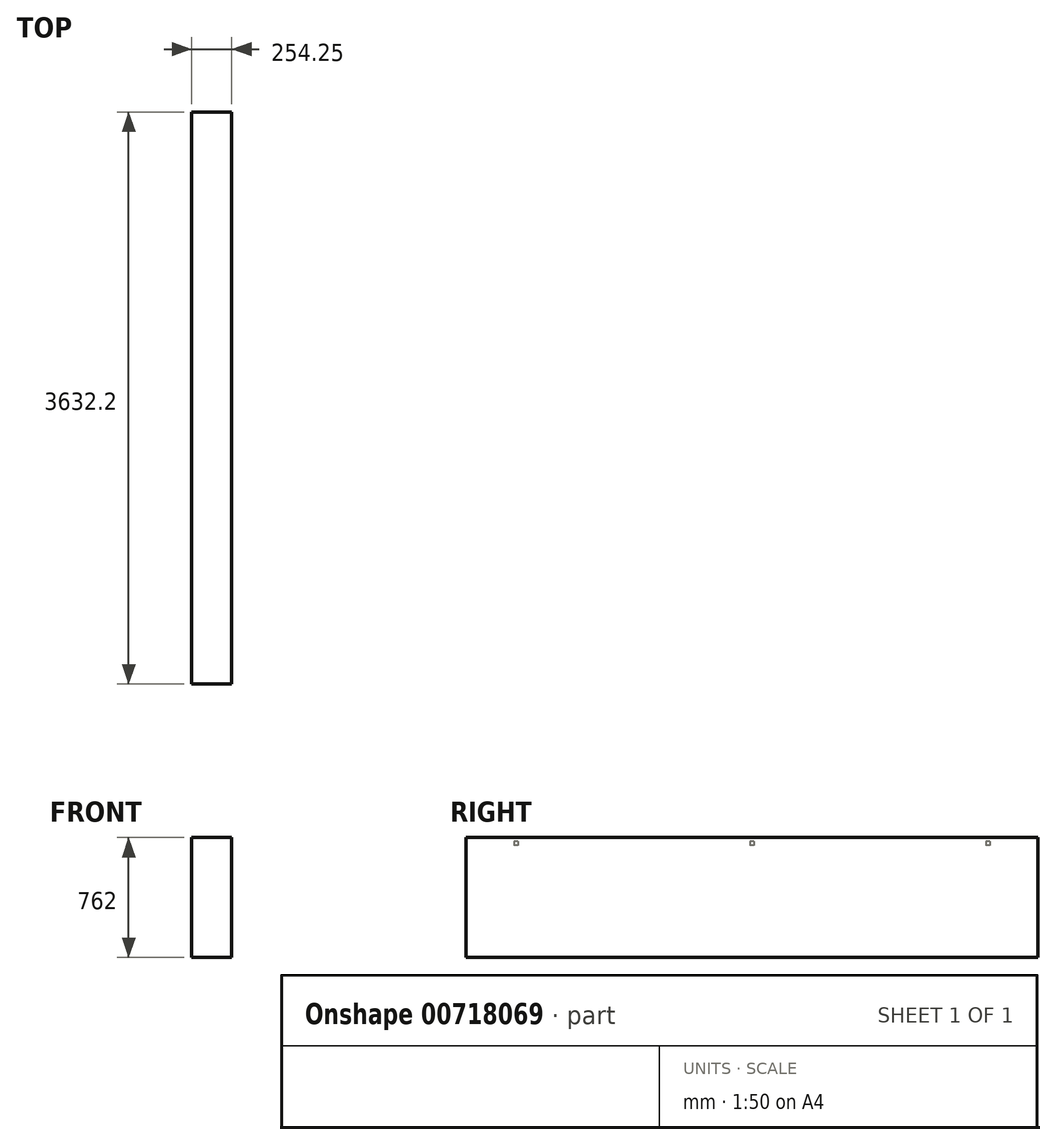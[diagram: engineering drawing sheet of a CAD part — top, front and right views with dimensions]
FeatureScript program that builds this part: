
annotation { "Feature Type Name" : "Feature", "Feature Type Description" : "" }
export const myFeature = defineFeature(function(context is Context, id is Id, definition is map)
    precondition{}
    {
        {
            var Q0;
            Q0=qCreatedBy(makeId("Front.planeOp"),FACE);
            var sketch = newSketch(context, id + "F0", { "sketchPlane" : qUnion([Q0])});
            skLineSegment(sketch, "E0.bottom", {"start": v(127, -381) * mm, "end": v(-127, -381) * mm});
            skLineSegment(sketch, "E0.top", {"start": v(127, 381) * mm, "end": v(-127, 381) * mm});
            skLineSegment(sketch, "E0.left", {"start": v(127, -381) * mm, "end": v(127, 381) * mm});
            skLineSegment(sketch, "E0.right", {"start": v(-127, -381) * mm, "end": v(-127, 381) * mm});
            skPoint(sketch, "E0.middle", {"position": v(0, 0) * mm});
            skSolve(sketch);
        }
        {
            var Q0;
            Q0 = qSketchRegion(id + "F0", true);
            extrude(context, id + "F1", {"entities" : qUnion([Q0]), "depth" : 3632.2 * mm, "offsetDistance" : 25.4 * mm});
        }
        {
            var Q0;
            Q0=makeQuery(id+"F1.opExtrude","SWEPT_FACE",FACE,{"disambiguationData":[OSD([sQuery(id+"F0.wireOp",EDGE,"E0.right")])]});
            var sketch = newSketch(context, id + "F2", { "sketchPlane" : qUnion([Q0])});
            skLineSegment(sketch, "E1.bottom", {"start": v(304.8, 355.6) * mm, "end": v(330.2, 355.6) * mm});
            skLineSegment(sketch, "E1.top", {"start": v(304.8, 330.2) * mm, "end": v(330.2, 330.2) * mm});
            skLineSegment(sketch, "E1.left", {"start": v(304.8, 355.6) * mm, "end": v(304.8, 330.2) * mm});
            skLineSegment(sketch, "E1.right", {"start": v(330.2, 355.6) * mm, "end": v(330.2, 330.2) * mm});
            skLineSegment(sketch, "E2.bottom", {"start": v(1803.4, 355.6) * mm, "end": v(1828.8, 355.6) * mm});
            skLineSegment(sketch, "E2.top", {"start": v(1803.4, 330.2) * mm, "end": v(1828.8, 330.2) * mm});
            skLineSegment(sketch, "E2.left", {"start": v(1803.4, 355.6) * mm, "end": v(1803.4, 330.2) * mm});
            skLineSegment(sketch, "E2.right", {"start": v(1828.8, 355.6) * mm, "end": v(1828.8, 330.2) * mm});
            skLineSegment(sketch, "E3.bottom", {"start": v(3302, 355.6) * mm, "end": v(3327.4, 355.6) * mm});
            skLineSegment(sketch, "E3.top", {"start": v(3302, 330.2) * mm, "end": v(3327.4, 330.2) * mm});
            skLineSegment(sketch, "E3.left", {"start": v(3302, 355.6) * mm, "end": v(3302, 330.2) * mm});
            skLineSegment(sketch, "E3.right", {"start": v(3327.4, 355.6) * mm, "end": v(3327.4, 330.2) * mm});
            skSolve(sketch);
        }
        {
            var Q0;
            Q0 = qSketchRegion(id + "F2", true);
            extrude(context, id + "F3", {"entities" : qUnion([Q0]), "operationType" : NewBodyOperationType.ADD, "depth" : 0.25 * mm, "offsetDistance" : 25.4 * mm});
        }
    });
